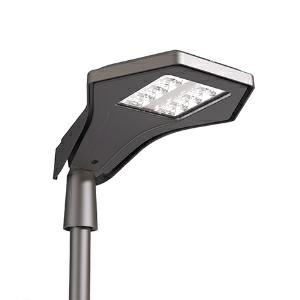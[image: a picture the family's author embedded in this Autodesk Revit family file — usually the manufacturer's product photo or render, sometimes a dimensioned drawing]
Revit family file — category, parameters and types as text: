
# Revit family: 3f_filippi_-_3f_manta_ampio_3f_filippi_-_7004_-_3f_manta_an_135-730_wide
name_source: partatom
category: Lighting Fixtures
units: mm (PartAtom-declared; Revit-internal decimal feet)

## family parameters
Cut with Voids When Loaded = No
Host = Face
Light Source = No
Part Type = Normal
Room Calculation Point = No
Round Connector Dimension = Use Diameter
Shared = No

## types (1)
- 3F Filippi - 3F Manta Ampio (1 x LED, 17458 lm, 149 W, 3000 K)
    Apparent Load = 149 VA
    Approval mark = CE
    CIE Flux Codes = 34 73 99 100 100
    Color Rendering = 70
    Color Temperature = 3000 K
    Control Gear = Electronic ballast
    Default Elevation = 1800 mm
    Description = ILLUMINOTECHNICAL
Luminous efficiency 100% (DLOR 100%, ULOR 0%).
Initial luminous flux of the luminaire 17458 lm.
Asymmetric distribution with wide bilateral.
BUG (Backlight, Uplight, Glare) IESNA TM-15: B3 U0 G2.
Luminous efficacy 117 lm/W.
Lifetime (L93/B10): 30000 h. (tq+25°C)
Lifetime (L90/B10): 50000 h. (tq+25°C)
Lifetime (L85/B10): 80000 h. (tq+25°C)
Lifetime (L80/B10): 100000 h. (tq+25°C)
Lifetime (L90/B20): 50000 h. (tq+45°C)
Sudden decreased luminous flux after 50000 hours: 0% (C0).
Photobiological safety in compliance with IEC/TR 62778: RG0 risk exempt, (IEC 62471).
In compliance with IEC/EN 62722-2-1 - IEC/EN 62717 standards.

SOURCE
Squared LED module 135W/730.
Source with special protection against aggressive chemically-volatile substances for standard LED technology.
Energy efficiency class (UE 2019/2020 - UE 2019/2015): E.
CIE 13.3 Colour rendering index: CRI >70 (R9 <50%).
IES TM-30 Fidelity Index: Rf = 72 Rg = 95.
CCT nominal colour temperature 3000 K.
Colour initial tolerance (MacAdam): SDCM 5.

MECHANICAL
Aerodynamically-shaped die-cast aluminium double-shell body for low wind resistance (frontal: 0.0446 m²; lateral: 0.0505 m²), equipped with fins to optimize the cooling of the internal components.
Shell closure using stainless steel screws on stainless steel bushings, with hinged opening for easy access to the wiring compartment, equipped with system against accidental closure.
Polyester powder coating with degreasing pre-treatment and phosphate layer deposit on the metal, UV stabilised, corrosion resistant, anthracite colour, salt spray resistance ISO 9227 >1000 h.
Parabolic cellular optics with total recovery, entirely made of semi-specular high reflection aluminium with titanium and magnesium surface treatment, to maintain optical performance over time.
Polyurethane foam seals, ecological, anti-aging, installed using a continuous automatic process with no joints.
VT extra transparent tempered glass diffuser, 4 mm thick, non-combustible, with Heat Soak Test (HST) thermal treatment, which drastically reduces the risk of spontaneous breakage.
Stainless steel internal and external screws.
Luminaire with limited surface temperature. - D - (EN 60598-2-24)
Dimensions: 660x440 mm, height 166 mm. Weight 11.5 kg.
IP66 protection degree.
Mechanical strength to impacts IK08 (5 joule).
Glow-wire test resistance 960°C.

ELECTRICAL
Halogen Free electronic wiring 230V-50/60Hz, power factor 0.97, THD <25%, constant output current, class I, 1 driver.
Power of the luminaire 149 W.
ENEC - CE.
Flicker: <5%.
Ambient temperature from -20°C to +45°C.
Temperature class T6 max 85°C.
Safety break switch to shut off the power supply when opening the device.
Insulation voltage 6kV via Sourge Protector.
SPD type 2+3 (combined) device to protect against voltage surges up to 10 kV in common and differential mode.
Thermal protection of the LED module via NTC sensor (Negative Temperature Coefficient).
M20x1.5 IP68 nylon cable gland for feeding input (cables with an min-max diameter 6-13mm).
Pressure compensating valve with anti-condensation effect.
Relative humidity UR: <85%.

INSTALLATION
Post-top / arm / wall.
Installation with always necessary "Pole fixing" accessory (see accessories).
All accessories dedicated to this product are available on the Catalog and on our website www.3F-Filippi.com.

ACCESSORIES
Pole mount in die-cast aluminium with the same paint treatment as the body (for Ø 60 mm and Ø 76 mm poles) equipped with special teeth for adjusting the inclination on the head of the device by ± 20° with an adjustment pitch of 5°.
Possibility of installing on vertical pole (pole head) and horizontal pole (arm).
Mounting on the device using the supplied stainless steel screws on self-locking stainless steel nuts.
A0439 - Pole mounting diameter 60 mm.
A0440 - Pole mounting diameter 76 mm.

APPLICATIONS
Outdoor environments, general lighting, work and roadway lighting, transit areas and building perimeters, parking lots, trade fairs.
Control of light pollution, in accordance with the legislative requirements in force.

LIGHT MANAGEMENT
Upon request, the appliance can be supplied with "Virtual Midnight" programming.

WARNING
Luminaire designed for disposal/recycling at end-of-life.
Replaceable (LED only) light source by a professional. Replaceable control gear by a professional.
    Height = 166 mm
    Lamp = 1 x LED
    Lamp Light Flux = 17458 lm
    Lamp Power = 149 W
    Lamp count = 1
    Length = 660 mm
    Lifetime = 50000 h
    Luminous efficacy = 117 lm/W
    Manufacturer = 3F Filippi
    ModVariant = No
    Model = 3F Filippi - 7004 - 3F Manta AN 135-730 WIDE
    Mounting Place = Pole
    Mounting Type = Pole top
    Number of Poles = 1
    OnlyDefault = Yes
    Power Factor = 1
    Product Name = 3F Filippi - 3F Manta Ampio
    Product group = street luminaire
    ProductGroupID = 15
    Protection Class = Protection class I
    Protection Degree = IP 66
    RLX_Detail_Level = 1
    RLX_Emergency_Light_Flux = 0 lm
    RLX_Emergency_Type = 0
    RLX_Emergency_Type_DB = No
    RlxData = <blob elided: 225233 chars, md5=76ec30c4>
    Socket = socket
    Standby Power = 0 W
    System Light Flux = 17458 lm
    System Power = 149 W
    Type Comments = Product without accessories
    Type Image = 3ffilippi_3f_manta_wide.jpg
    URL = http://relux.com
    VarID = ---
    Voltage = 0 V
    Weight = 0.00 kg
    Width = 440 mm

## geometry (parser evidence)
native form markers: Blend x4, Sweep x13
no freeform markers — native parametric forms only
